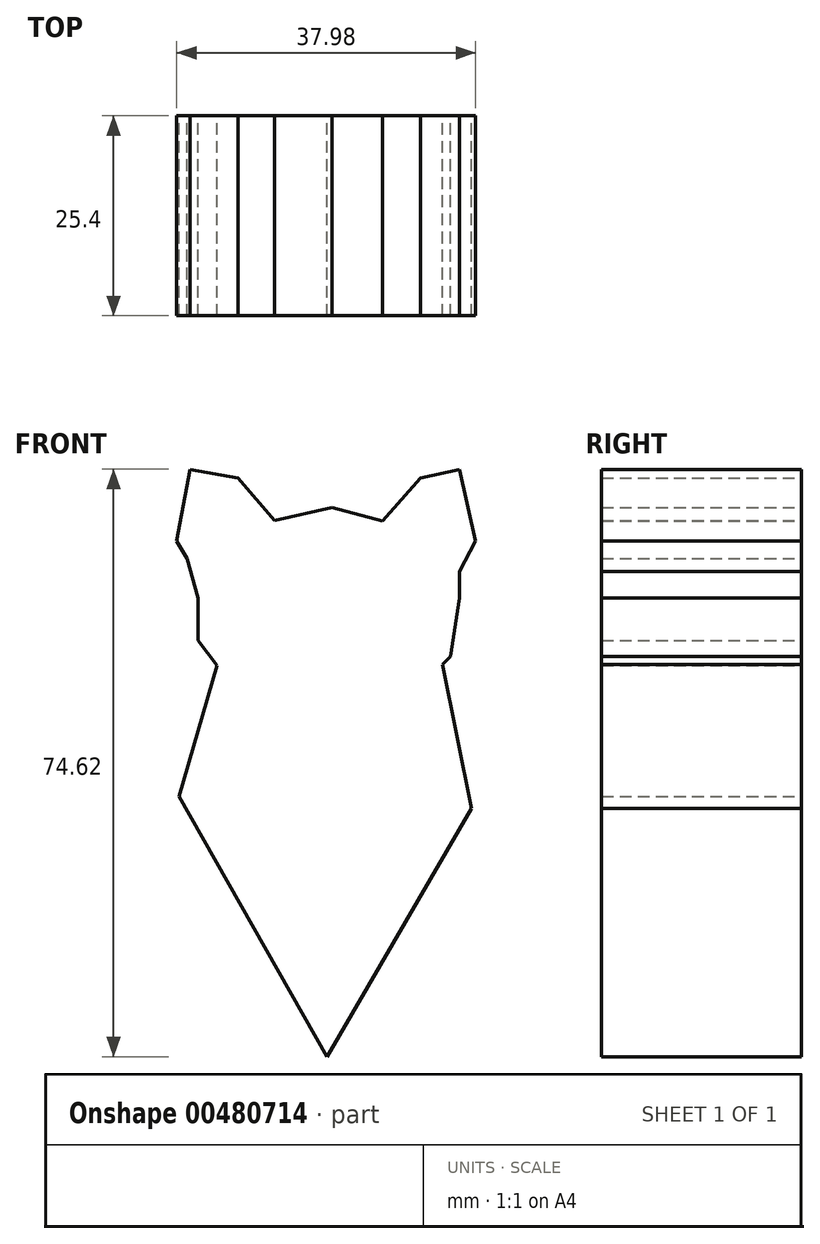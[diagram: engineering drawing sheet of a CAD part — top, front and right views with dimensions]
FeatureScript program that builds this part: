
annotation { "Feature Type Name" : "Feature", "Feature Type Description" : "" }
export const myFeature = defineFeature(function(context is Context, id is Id, definition is map)
    precondition{}
    {
        {
            var Q0;
            Q0=qCreatedBy(makeId("Front.planeOp"),FACE);
            var sketch = newSketch(context, id + "F0", { "sketchPlane" : qUnion([Q0])});
            skLineSegment(sketch, "E0", {"start": v(-13.74, 43.1) * mm, "end": v(-15.43, 34) * mm});
            skLineSegment(sketch, "E1", {"start": v(-15.43, 34) * mm, "end": v(-14.08, 31.8) * mm});
            skLineSegment(sketch, "E2", {"start": v(-14.08, 31.8) * mm, "end": v(-12.73, 26.73) * mm});
            skLineSegment(sketch, "E3", {"start": v(-12.73, 26.73) * mm, "end": v(-12.73, 25.21) * mm});
            skLineSegment(sketch, "E4", {"start": v(-12.73, 25.21) * mm, "end": v(-12.73, 21.33) * mm});
            skLineSegment(sketch, "E5", {"start": v(-12.73, 21.33) * mm, "end": v(-7.83, 15.08) * mm});
            skLineSegment(sketch, "E6", {"start": v(-7.83, 15.08) * mm, "end": v(-4.8, 9.34) * mm});
            skLineSegment(sketch, "E7", {"start": v(-4.8, 9.34) * mm, "end": v(-1.59, 5.46) * mm});
            skLineSegment(sketch, "E8", {"start": v(-1.59, 5.46) * mm, "end": v(3.65, 4.11) * mm});
            skLineSegment(sketch, "E9", {"start": v(3.65, 4.11) * mm, "end": v(7.02, 4.11) * mm});
            skLineSegment(sketch, "E10", {"start": v(7.02, 4.11) * mm, "end": v(10.9, 7.82) * mm});
            skLineSegment(sketch, "E11", {"start": v(10.9, 7.82) * mm, "end": v(14.96, 15.08) * mm});
            skLineSegment(sketch, "E12", {"start": v(14.96, 15.08) * mm, "end": v(19.35, 19.3) * mm});
            skLineSegment(sketch, "E13", {"start": v(19.35, 19.3) * mm, "end": v(20.53, 26.73) * mm});
            skLineSegment(sketch, "E14", {"start": v(20.53, 26.73) * mm, "end": v(20.53, 30.1) * mm});
            skLineSegment(sketch, "E15", {"start": v(20.53, 30.1) * mm, "end": v(22.55, 34) * mm});
            skLineSegment(sketch, "E16", {"start": v(22.55, 34) * mm, "end": v(20.53, 43.1) * mm});
            skLineSegment(sketch, "E17", {"start": v(20.53, 43.1) * mm, "end": v(15.54, 42) * mm});
            skLineSegment(sketch, "E18", {"start": v(15.54, 42) * mm, "end": v(10.74, 36.53) * mm});
            skLineSegment(sketch, "E19", {"start": v(10.74, 36.53) * mm, "end": v(4.32, 38.22) * mm});
            skLineSegment(sketch, "E20", {"start": v(4.32, 38.22) * mm, "end": v(-3.03, 36.59) * mm});
            skLineSegment(sketch, "E21", {"start": v(-3.03, 36.59) * mm, "end": v(-7.66, 42) * mm});
            skLineSegment(sketch, "E22", {"start": v(-7.66, 42) * mm, "end": v(-13.74, 43.1) * mm});
            skLineSegment(sketch, "E23", {"start": v(-10.28, 18.2) * mm, "end": v(-15.1, 1.58) * mm});
            skLineSegment(sketch, "E24", {"start": v(-15.1, 1.58) * mm, "end": v(3.65, -31.51) * mm});
            skLineSegment(sketch, "E25", {"start": v(3.65, -31.51) * mm, "end": v(22.05, 0) * mm});
            skLineSegment(sketch, "E26", {"start": v(22.05, 0) * mm, "end": v(18.32, 18.32) * mm});
            skSolve(sketch);
        }
        {
            var Q0;
            Q0=makeQuery(id+"F0.imprint","IMPRINT",FACE,{"disambiguationData":[TD([[makeQuery(id+"F0.imprint","IMPRINT",EDGE,{"derivedFrom":sQuery(id+"F0.wireOp",EDGE,"E0")}),1.0]])]});
            var Q1;
            {var subQ4=sQuery(id+"F0.wireOp",EDGE,"E6");Q1=makeQuery(id+"F0.imprint","IMPRINT",FACE,{"disambiguationData":[TD([[makeQuery(id+"F0.imprint","IMPRINT",EDGE,{"derivedFrom":subQ4}),-1.0]])]});}
            extrude(context, id + "F1", {"entities" : qUnion([Q0, Q1]), "depth" : 25.4 * mm});
        }
    });
